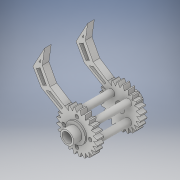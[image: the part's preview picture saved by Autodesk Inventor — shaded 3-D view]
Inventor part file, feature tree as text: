
AUTODESK INVENTOR PART (.ipt)
format: ipt  version: 2017 (Build 210142000, 142)  size: 652,288 bytes
history: native  units: in
note: dims shown in document units (in); Inventor stores cm internally (conversion verified against a paired STEP export)
features: extrude x30, sketch x30
ambient origin geometry x8: Origin, YZ Plane, XZ Plane, XY Plane, X Axis, Y Axis, Z Axis, Center Point
bodies: Solid1 (feature_tree)
feature tree (60):
  extrude  "Extrusion1"  Depth=0.5in
  extrude  "Extrusion2"  TaperAngle=150.0deg  [1 undecoded]
  extrude  "Extrusion3"  Depth=0.2in TaperAngle=0.0deg
  extrude  "Extrusion4"  TaperAngle=30.0deg  [1 undecoded]
  extrude  "Extrusion5"  TaperAngle=60.0deg  [1 undecoded]
  extrude  "Extrusion6"  Depth=0.2in TaperAngle=0.0deg
  extrude  "Extrusion7"  Depth=0.2in
  extrude  "Extrusion8"  Depth=0.2in TaperAngle=0.0deg
  extrude  "Extrusion9"  Depth=0.2in TaperAngle=0.0deg
  extrude  "Extrusion10"  Depth=0.4in
  extrude  "Extrusion11"  Depth=0.4in
  extrude  "Extrusion12"  Depth=0.4in
  extrude  "Extrusion13"  Depth=0.4in
  extrude  "Extrusion14"  Depth=0.2in TaperAngle=0.0deg
  extrude  "Extrusion15"  TaperAngle=60.0deg  [1 undecoded]
  extrude  "Extrusion16"  Depth=0.5in
  extrude  "Extrusion17"  Depth=0.2in TaperAngle=0.0deg
  extrude  "Extrusion18"  TaperAngle=135.0deg  [1 undecoded]
  extrude  "Extrusion19"  TaperAngle=45.0deg  [1 undecoded]
  extrude  "Extrusion20"  TaperAngle=135.0deg  [1 undecoded]
  extrude  "Extrusion21"  Depth=0.2in
  extrude  "Extrusion22"  Depth=1.1in TaperAngle=0.0deg
  extrude  "Extrusion23"  Depth=0.2in TaperAngle=0.0deg
  extrude  "Extrusion24"  Depth=0.2in TaperAngle=0.0deg
  extrude  "Extrusion25"  Depth=0.2in TaperAngle=0.0deg
  extrude  "Extrusion26"  Depth=0.2in TaperAngle=0.0deg
  extrude  "Extrusion27"  Depth=0.2in TaperAngle=0.0deg
  extrude  "Extrusion28"  Depth=0.2in TaperAngle=0.0deg
  extrude  "Extrusion29"  Depth=2.0in TaperAngle=0.0deg
  extrude  "Extrusion30"  Depth=0.05in TaperAngle=0.0deg
  sketch  "Sketch1"  dims[d0=0.5in d1=0.5in]
  sketch  "Sketch2"  dims[d2=15.0deg d3=150.0deg]
  sketch  "Sketch3"  dims[d4=30.0deg d5=0.2in d6=0.0in]
  sketch  "Sketch4"  dims[d7=0.5in d8=30.0deg]
  sketch  "Sketch5"  dims[d9=60.0deg d10=60.0deg]
  sketch  "Sketch6"  dims[d11=0.2in d12=0.0in d13=0.2in d14=0.0in]
  sketch  "Sketch7"  dims[d15=0.2in d16=0.0in d17=1.0in]
  sketch  "Sketch8"  dims[d18=0.2in d19=0.0in d20=0.2in d21=0.0in]
  sketch  "Sketch9"  dims[d22=0.3in d23=0.2in d24=0.0in]
  sketch  "Sketch10"  dims[d25=0.2in d26=0.0in d27=0.4in]
  sketch  "Sketch11"  dims[d28=0.11in d29=0.4in]
  sketch  "Sketch12"  dims[d30=0.11in d31=0.4in]
  sketch  "Sketch13"  dims[d32=0.4in d33=0.11in]
  sketch  "Sketch14"  dims[d34=0.11in d35=0.2in d36=0.0in]
  sketch  "Sketch15"  dims[d37=1.5in d38=60.0deg]
  sketch  "Sketch16"  dims[d39=30.0deg d40=0.5in]
  sketch  "Sketch17"  dims[d41=150.0deg d42=0.2in d43=0.0in]
  sketch  "Sketch18"  dims[d44=0.2in d45=0.0in d46=135.0deg]
  sketch  "Sketch19"  dims[d47=0.2in d48=45.0deg]
  sketch  "Sketch20"  dims[d49=45.0deg d50=135.0deg]
  sketch  "Sketch21"  dims[d51=0.2in d52=0.2in]
  sketch  "Sketch22"  dims[d53=0.2in d54=1.1in d55=0.0in]
  sketch  "Sketch23"  dims[d56=30.0deg d57=0.2in d58=0.0in]
  sketch  "Sketch24"  dims[d59=0.2in d60=0.0in d61=0.2in d62=0.0in]
  sketch  "Sketch25"  dims[d63=0.2in d64=0.0in d65=0.2in d66=0.0in]
  sketch  "Sketch26"  dims[d67=0.2in d68=0.0in d69=0.2in d70=0.0in]
  sketch  "Sketch27"  dims[d71=0.3in d72=0.2in d73=0.0in]
  sketch  "Sketch28"  dims[d74=0.2in d75=0.0in d76=2.0in d77=0.0in]
  sketch  "Sketch29"  dims[d78=2.0in d79=0.0in d80=2.0in d81=0.0in]
  sketch  "Sketch30"  dims[d82=0.6in d83=0.05in d84=0.0in d85=0.4in d86=0.25in d87=0.0in d88=0.3in d89=1.0in d90=0.0in d91=0.6in d92=0.05in d93=0.0in d94=0.4in d95=0.25in d96=0.0in d97=0.3in d98=1.0in d99=0.0in]
note: 7 required parameter values undecoded (feature->parameter linkage not recoverable at this tier; creation-order binding heuristic only, values carry confidence <= 0.55)
